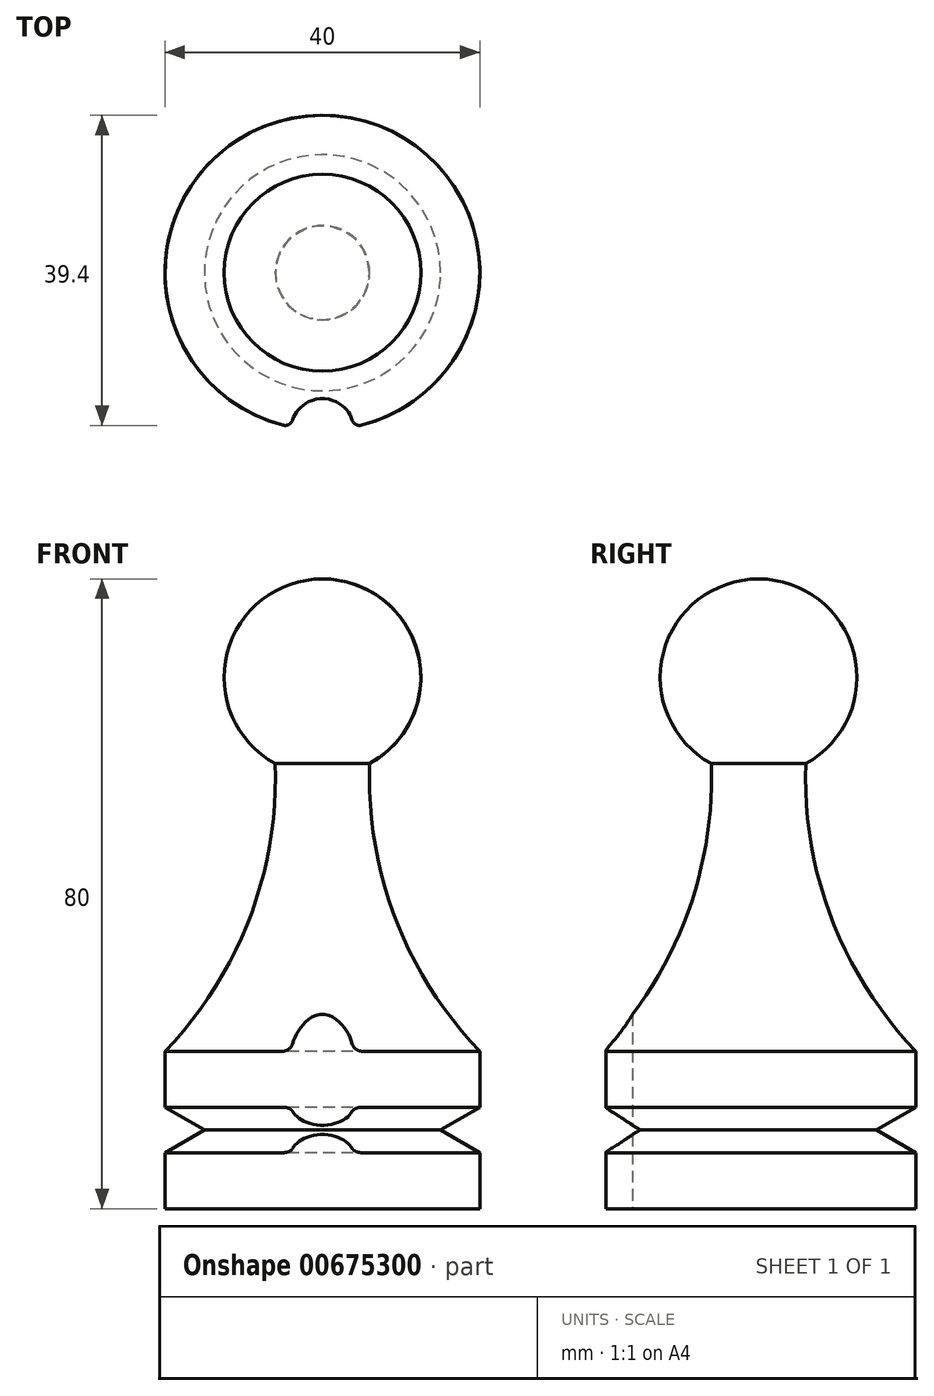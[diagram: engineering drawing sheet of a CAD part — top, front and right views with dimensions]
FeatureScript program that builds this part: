
annotation { "Feature Type Name" : "Feature", "Feature Type Description" : "" }
export const myFeature = defineFeature(function(context is Context, id is Id, definition is map)
    precondition{}
    {
        {
            var Q0;
            Q0=qCreatedBy(makeId("Front.planeOp"),FACE);
            var sketch = newSketch(context, id + "F0", { "sketchPlane" : qUnion([Q0])});
            skLineSegment(sketch, "E0", {"start": v(20, 0) * mm, "end": v(20, 7.11) * mm});
            skLineSegment(sketch, "E1", {"start": v(15, 10) * mm, "end": v(20, 7.11) * mm});
            skLineSegment(sketch, "E2", {"start": v(20, 12.89) * mm, "end": v(15, 10) * mm});
            skLineSegment(sketch, "E3", {"start": v(20, 12.89) * mm, "end": v(20, 20) * mm});
            skArc(sketch, "E4", {"start": v(6, 56.53) * mm, "mid": v(9.28, 36.84) * mm, "end": v(20, 20) * mm});
            skArc(sketch, "E5", {"start": v(6, 56.53) * mm, "mid": v(12.11, 70.6) * mm, "end": v(0, 80) * mm});
            skLineSegment(sketch, "E6", {"start": v(0, 80) * mm, "end": v(0, 0) * mm});
            skLineSegment(sketch, "E7", {"start": v(0, 0) * mm, "end": v(20, 0) * mm});
            skSolve(sketch);
        }
        {
            var Q0;
            Q0=makeQuery(id+"F0.imprint","IMPRINT",FACE,{"disambiguationData":[TD([[makeQuery(id+"F0.imprint","IMPRINT",EDGE,{"derivedFrom":sQuery(id+"F0.wireOp",EDGE,"E0")}),1.0]])]});
            var Q1;
            Q1=sQuery(id+"F0.wireOp",EDGE,"E6");
            revolve(context, id + "F1", {"entities" : qUnion([Q0]), "axis" : qUnion([Q1]), "revolveType" : RevolveType.FULL});
        }
        {
            var Q0;
            Q0=makeQuery(id+"F1.opRevolve","SWEPT_FACE",FACE,{"disambiguationData":[OSD([sQuery(id+"F0.wireOp",EDGE,"E7")])]});
            var sketch = newSketch(context, id + "F2", { "sketchPlane" : qUnion([Q0])});
            skCircle(sketch, "E8", {"center": v(0, 20) * mm, "radius": 4 * mm});
            skSolve(sketch);
        }
        {
            var Q0;
            Q0 = qSketchRegion(id + "F2", true);
            extrude(context, id + "F3", {"entities" : qUnion([Q0]), "operationType" : NewBodyOperationType.REMOVE, "oppositeDirection" : true, "depth" : 30 * mm, "offsetDistance" : 25 * mm});
        }
        {
            var Q0;
            Q0=makeQuery(id+"F3.boolean.opBoolean","INTERSECT",EDGE,{"disambiguationData":[OD(0.0)],"derivedFrom":[makeQuery(id+"F1.opRevolve","SWEPT_FACE",FACE,{"disambiguationData":[OSD([sQuery(id+"F0.wireOp",EDGE,"E3")])]}),makeQuery(id+"F3.opExtrude","SWEPT_FACE",FACE,{"disambiguationData":[OSD([sQuery(id+"F2.wireOp",EDGE,"E8")])]})]});
            var Q1;
            Q1=makeQuery(id+"F3.boolean.opBoolean","INTERSECT",EDGE,{"disambiguationData":[OD(1.0)],"derivedFrom":[makeQuery(id+"F1.opRevolve","SWEPT_FACE",FACE,{"disambiguationData":[OSD([sQuery(id+"F0.wireOp",EDGE,"E3")])]}),makeQuery(id+"F3.opExtrude","SWEPT_FACE",FACE,{"disambiguationData":[OSD([sQuery(id+"F2.wireOp",EDGE,"E8")])]})]});
            var Q2;
            Q2=makeQuery(id+"F3.boolean.opBoolean","INTERSECT",EDGE,{"disambiguationData":[OD(0.0)],"derivedFrom":[makeQuery(id+"F1.opRevolve","SWEPT_FACE",FACE,{"disambiguationData":[OSD([sQuery(id+"F0.wireOp",EDGE,"E0")])]}),makeQuery(id+"F3.opExtrude","SWEPT_FACE",FACE,{"disambiguationData":[OSD([sQuery(id+"F2.wireOp",EDGE,"E8")])]})]});
            var Q3;
            Q3=makeQuery(id+"F3.boolean.opBoolean","INTERSECT",EDGE,{"disambiguationData":[OD(1.0)],"derivedFrom":[makeQuery(id+"F1.opRevolve","SWEPT_FACE",FACE,{"disambiguationData":[OSD([sQuery(id+"F0.wireOp",EDGE,"E0")])]}),makeQuery(id+"F3.opExtrude","SWEPT_FACE",FACE,{"disambiguationData":[OSD([sQuery(id+"F2.wireOp",EDGE,"E8")])]})]});
            fillet(context, id + "F4", {"entities" : qUnion([Q0, Q1, Q2, Q3]), "radius" : 1 * mm, "tangentPropagation" : true, "allowEdgeOverflow" : false});
        }
    });
